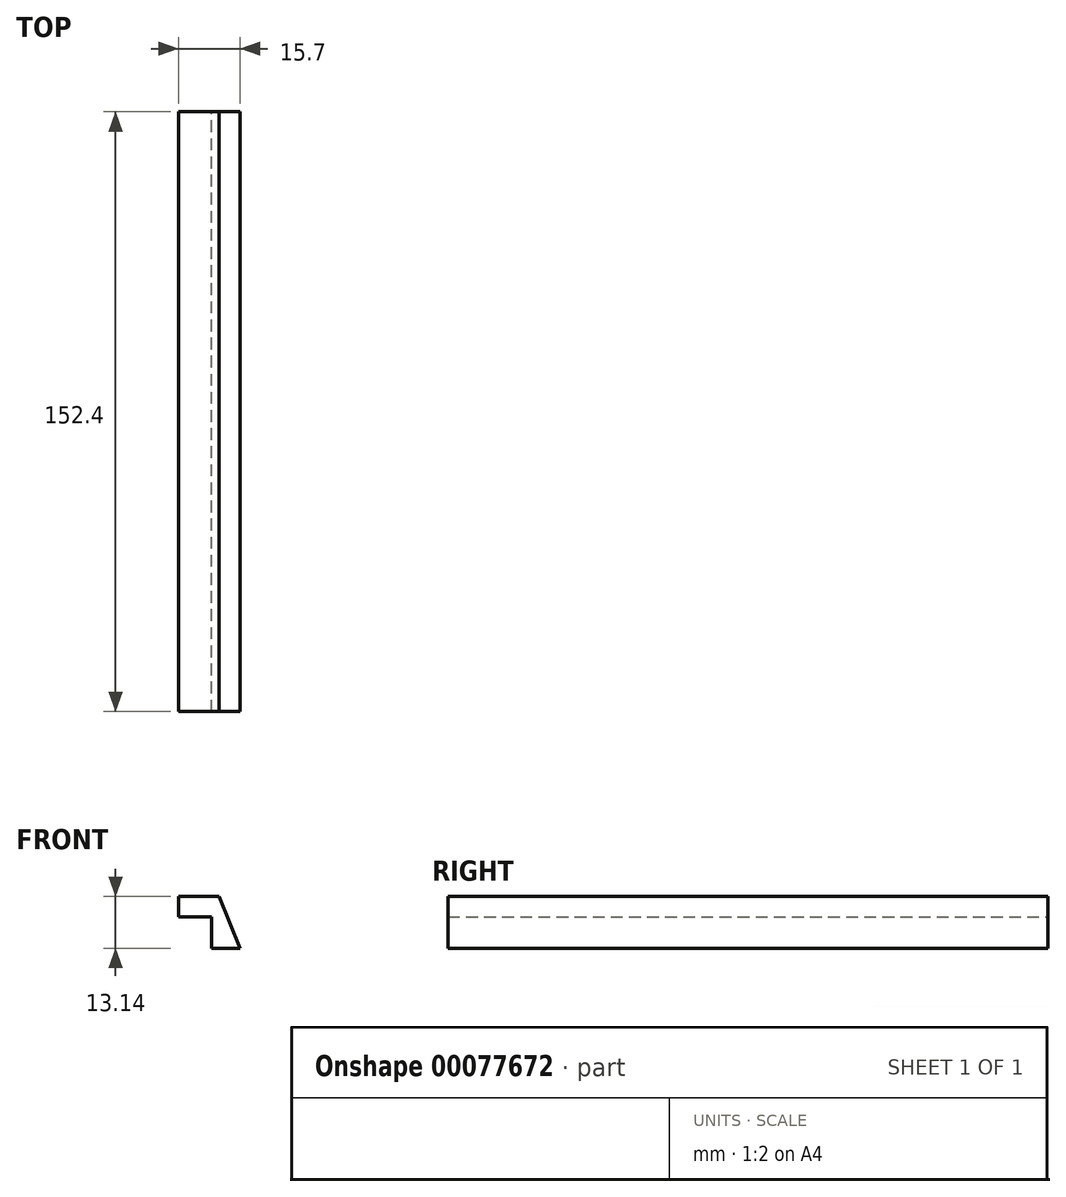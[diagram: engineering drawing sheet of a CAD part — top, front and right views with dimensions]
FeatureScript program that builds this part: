
annotation { "Feature Type Name" : "Feature", "Feature Type Description" : "" }
export const myFeature = defineFeature(function(context is Context, id is Id, definition is map)
    precondition{}
    {
        {
            var Q0;
            Q0=qCreatedBy(makeId("Front.planeOp"),FACE);
            var sketch = newSketch(context, id + "F0", { "sketchPlane" : qUnion([Q0])});
            skLineSegment(sketch, "E0", {"start": v(-7.85, 1.37) * mm, "end": v(0.54, 1.37) * mm});
            skLineSegment(sketch, "E1", {"start": v(0.54, -6.57) * mm, "end": v(0.54, 1.37) * mm});
            skLineSegment(sketch, "E2", {"start": v(-7.85, 1.37) * mm, "end": v(-7.85, 6.57) * mm});
            skLineSegment(sketch, "E3", {"start": v(-7.85, 6.57) * mm, "end": v(2.46, 6.57) * mm});
            skLineSegment(sketch, "E4", {"start": v(7.85, -6.57) * mm, "end": v(0.54, -6.57) * mm});
            skLineSegment(sketch, "E5", {"start": v(2.46, 6.57) * mm, "end": v(7.85, -6.57) * mm});
            skLineSegment(sketch, "E6", {"start": v(0.54, 1.37) * mm, "end": v(0.54, -6.57) * mm});
            skSolve(sketch);
        }
        {
            var Q0;
            Q0=makeQuery(id+"F0.imprint","IMPRINT",FACE,{"disambiguationData":[TD([[makeQuery(id+"F0.imprint","IMPRINT",EDGE,{"derivedFrom":sQuery(id+"F0.wireOp",EDGE,"E2")}),-1.0]])]});
            extrude(context, id + "F1", {"entities" : qUnion([Q0]), "depth" : 152.4 * mm});
        }
    });
